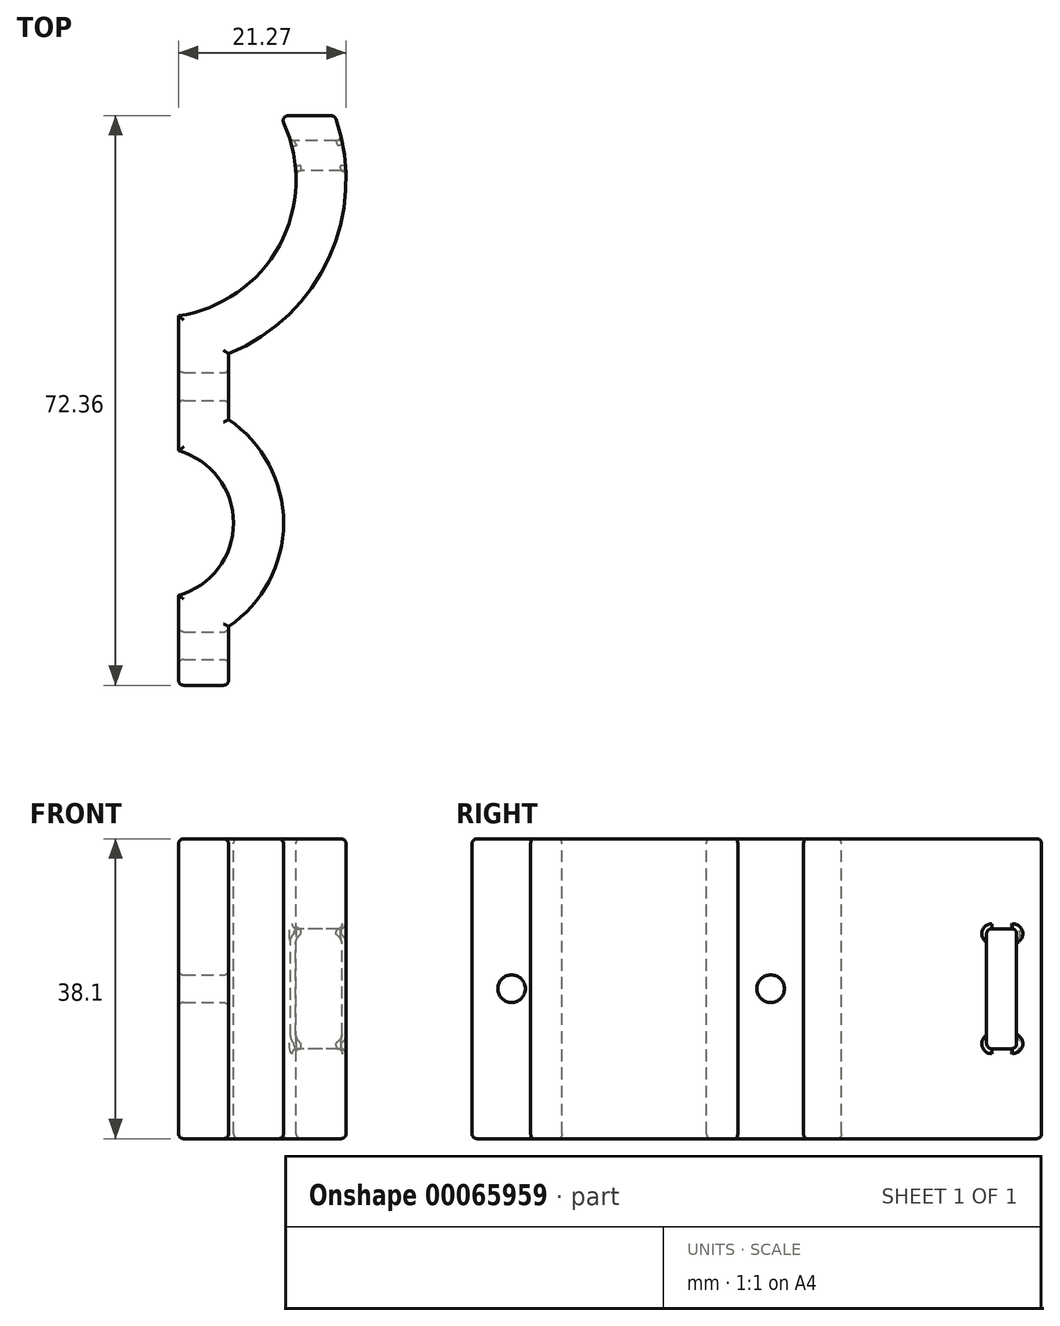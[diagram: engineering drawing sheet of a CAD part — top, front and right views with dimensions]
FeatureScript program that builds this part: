
annotation { "Feature Type Name" : "Feature", "Feature Type Description" : "" }
export const myFeature = defineFeature(function(context is Context, id is Id, definition is map)
    precondition{}
    {
        {
            var Q0;
            Q0=qCreatedBy(makeId("Top.planeOp"),FACE);
            var sketch = newSketch(context, id + "F0", { "sketchPlane" : qUnion([Q0])});
            skArc(sketch, "E0", {"start": v(0, 9.53) * mm, "mid": v(1.28, 9.44) * mm, "end": v(2.54, 9.18) * mm, "construction": true});
            skArc(sketch, "E1", {"start": v(0, 26.14) * mm, "mid": v(1.27, 26.19) * mm, "end": v(2.54, 26.33) * mm, "construction": true});
            skLineSegment(sketch, "E2", {"start": v(0, 43.6) * mm, "end": v(16.4, 49.57) * mm, "construction": true});
            skLineSegment(sketch, "E3", {"start": v(2.54, 26.33) * mm, "end": v(2.54, 9.18) * mm});
            skArc(sketch, "E4", {"start": v(16.4, 49.57) * mm, "mid": v(10.02, 57.9) * mm, "end": v(0, 61.06) * mm, "construction": true});
            skArc(sketch, "E5", {"start": v(2.54, 26.33) * mm, "mid": v(15.57, 35.7) * mm, "end": v(15.45, 51.75) * mm});
            skArc(sketch, "E6", {"start": v(2.54, 9.18) * mm, "mid": v(9.53, 0) * mm, "end": v(2.54, -9.18) * mm});
            skLineSegment(sketch, "E7", {"start": v(2.54, 9.18) * mm, "end": v(2.54, -9.18) * mm, "construction": true});
            skArc(sketch, "E8", {"start": v(2.54, -9.18) * mm, "mid": v(1.28, -9.44) * mm, "end": v(0, -9.53) * mm});
            skArc(sketch, "E9.0", {"start": v(8.9, 21.51) * mm, "mid": v(21.75, 33.9) * mm, "end": v(22.38, 51.75) * mm});
            skLineSegment(sketch, "E9.1", {"start": v(8.9, 21.51) * mm, "end": v(8.9, 13.15) * mm});
            skArc(sketch, "E9.2", {"start": v(8.9, 13.15) * mm, "mid": v(15.88, 0) * mm, "end": v(8.9, -13.15) * mm});
            skLineSegment(sketch, "E10", {"start": v(22.38, 51.75) * mm, "end": v(15.45, 51.75) * mm});
            skLineSegment(sketch, "E11", {"start": v(2.54, -9.18) * mm, "end": v(2.54, -20.61) * mm});
            skLineSegment(sketch, "E12.0", {"start": v(8.9, -13.15) * mm, "end": v(8.9, -20.61) * mm});
            skLineSegment(sketch, "E13", {"start": v(2.54, -20.61) * mm, "end": v(8.9, -20.61) * mm});
            skSolve(sketch);
        }
        {
            var Q0;
            Q0 = qSketchRegion(id + "F0", true);
            extrude(context, id + "F1", {"entities" : qUnion([Q0]), "oppositeDirection" : true, "depth" : 38.1 * mm});
        }
        {
            var Q0;
            Q0=makeQuery(id+"F1.opExtrude","SWEPT_FACE",FACE,{"disambiguationData":[OSD([sQuery(id+"F0.wireOp",EDGE,"E9.1")])]});
            var sketch = newSketch(context, id + "F2", { "sketchPlane" : qUnion([Q0])});
            skLineSegment(sketch, "E14", {"start": v(17.33, 0) * mm, "end": v(17.33, -38.1) * mm, "construction": true});
            skLineSegment(sketch, "E15", {"start": v(13.15, -19.05) * mm, "end": v(21.51, -19.05) * mm, "construction": true});
            skPoint(sketch, "E16", {"position": v(17.33, -19.05) * mm});
            skCircle(sketch, "E17", {"center": v(17.33, -19.05) * mm, "radius": 1.75 * mm});
            skSolve(sketch);
        }
        {
            var Q0;
            Q0 = qSketchRegion(id + "F2", true);
            extrude(context, id + "F3", {"entities" : qUnion([Q0]), "operationType" : NewBodyOperationType.REMOVE, "endBound" : BoundingType.UP_TO_NEXT, "oppositeDirection" : true, "depth" : 25.4 * mm});
        }
        {
            var Q0;
            Q0=qCreatedBy(makeId("Right.planeOp"),FACE);
            var sketch = newSketch(context, id + "F4", { "sketchPlane" : qUnion([Q0])});
            skLineSegment(sketch, "E18.0", {"start": v(21.51, 0) * mm, "end": v(21.51, -38.1) * mm, "construction": true});
            skLineSegment(sketch, "E19", {"start": v(71.82, -19.05) * mm, "end": v(21.51, -19.05) * mm, "construction": true});
            skPoint(sketch, "E19.endSnap0", {"position": v(21.51, -19.05) * mm});
            skLineSegment(sketch, "E20.rect.bottom", {"start": v(48.57, -11.43) * mm, "end": v(44.76, -11.43) * mm});
            skLineSegment(sketch, "E20.rect.top", {"start": v(48.57, -26.67) * mm, "end": v(44.76, -26.67) * mm});
            skLineSegment(sketch, "E20.rect.left", {"start": v(48.57, -11.43) * mm, "end": v(48.57, -26.67) * mm});
            skLineSegment(sketch, "E20.rect.right", {"start": v(44.76, -11.43) * mm, "end": v(44.76, -26.67) * mm});
            skPoint(sketch, "E20.rect.middle", {"position": v(46.67, -19.05) * mm});
            skSolve(sketch);
        }
        {
            var Q0;
            Q0 = qSketchRegion(id + "F4", true);
            extrude(context, id + "F5", {"entities" : qUnion([Q0]), "operationType" : NewBodyOperationType.REMOVE, "endBound" : BoundingType.THROUGH_ALL, "depth" : 25.4 * mm});
        }
        {
            var Q0;
            Q0=makeQuery(id+"F1.opExtrude","SWEPT_FACE",FACE,{"disambiguationData":[OSD([sQuery(id+"F0.wireOp",EDGE,"E12.0")])]});
            var sketch = newSketch(context, id + "F6", { "sketchPlane" : qUnion([Q0])});
            skLineSegment(sketch, "E21", {"start": v(-13.15, -19.05) * mm, "end": v(-13.15, -19.05) * mm});
            skLineSegment(sketch, "E22", {"start": v(-15.58, 0) * mm, "end": v(-15.58, -38.1) * mm, "construction": true});
            skPoint(sketch, "E23", {"position": v(-15.58, -19.05) * mm});
            skCircle(sketch, "E24", {"center": v(-15.58, -19.05) * mm, "radius": 1.75 * mm});
            skSolve(sketch);
        }
        {
            var Q0;
            Q0=makeQuery(id+"F6.imprint","IMPRINT",FACE,{"disambiguationData":[TD([[makeQuery(id+"F6.imprint","IMPRINT",EDGE,{"derivedFrom":sQuery(id+"F6.wireOp",EDGE,"E24")}),1.0]])]});
            var Q1;
            Q1=sQuery(id+"F6.wireOp",EDGE,"E24");
            extrude(context, id + "F7", {"entities" : qUnion([Q0]), "operationType" : NewBodyOperationType.REMOVE, "surfaceEntities" : qUnion([Q1]), "endBound" : BoundingType.THROUGH_ALL, "oppositeDirection" : true, "depth" : 25.4 * mm});
        }
        {
            var Q0;
            Q0=makeQuery(id+"F1.opExtrude","CAP_FACE",FACE,{"disambiguationData":[OSD([sQuery(id+"F0.wireOp",EDGE,"E3"),sQuery(id+"F0.wireOp",EDGE,"E5"),sQuery(id+"F0.wireOp",EDGE,"E6"),sQuery(id+"F0.wireOp",EDGE,"E9.0"),sQuery(id+"F0.wireOp",EDGE,"E9.1"),sQuery(id+"F0.wireOp",EDGE,"E9.2"),sQuery(id+"F0.wireOp",EDGE,"E10"),sQuery(id+"F0.wireOp",EDGE,"E11"),sQuery(id+"F0.wireOp",EDGE,"E12.0"),sQuery(id+"F0.wireOp",EDGE,"E13")])],"isStart":true});
            var Q1;
            Q1=makeQuery(id+"F1.opExtrude","CAP_FACE",FACE,{"disambiguationData":[OSD([sQuery(id+"F0.wireOp",EDGE,"E3"),sQuery(id+"F0.wireOp",EDGE,"E5"),sQuery(id+"F0.wireOp",EDGE,"E6"),sQuery(id+"F0.wireOp",EDGE,"E9.0"),sQuery(id+"F0.wireOp",EDGE,"E9.1"),sQuery(id+"F0.wireOp",EDGE,"E9.2"),sQuery(id+"F0.wireOp",EDGE,"E10"),sQuery(id+"F0.wireOp",EDGE,"E11"),sQuery(id+"F0.wireOp",EDGE,"E12.0"),sQuery(id+"F0.wireOp",EDGE,"E13")])],"isStart":false});
            var Q2;
            Q2=makeQuery(id+"F1.opExtrude","SWEPT_FACE",FACE,{"disambiguationData":[OSD([sQuery(id+"F0.wireOp",EDGE,"E13")])]});
            var Q3;
            Q3=makeQuery(id+"F1.opExtrude","SWEPT_FACE",FACE,{"disambiguationData":[OSD([sQuery(id+"F0.wireOp",EDGE,"E10")])]});
            var Q4;
            Q4=makeQuery(id+"F3.boolean.opBoolean","COPY",FACE,{"derivedFrom":makeQuery(id+"F3.opExtrude","SWEPT_FACE",FACE,{"disambiguationData":[OSD([sQuery(id+"F2.wireOp",EDGE,"E17")])]})});
            var Q5;
            Q5=makeQuery(id+"F7.boolean.opBoolean","COPY",FACE,{"derivedFrom":makeQuery(id+"F7.opExtrude","SWEPT_FACE",FACE,{"disambiguationData":[OSD([sQuery(id+"F6.wireOp",EDGE,"E24")])]})});
            var Q6;
            Q6=makeQuery(id+"F5.boolean.opBoolean","COPY",FACE,{"derivedFrom":makeQuery(id+"F5.opExtrude","SWEPT_FACE",FACE,{"disambiguationData":[OSD([sQuery(id+"F4.wireOp",EDGE,"E20.rect.bottom")])]})});
            var Q7;
            Q7=makeQuery(id+"F5.boolean.opBoolean","COPY",FACE,{"derivedFrom":makeQuery(id+"F5.opExtrude","SWEPT_FACE",FACE,{"disambiguationData":[OSD([sQuery(id+"F4.wireOp",EDGE,"E20.rect.top")])]})});
            fillet(context, id + "F8", {"entities" : qUnion([Q0, Q1, Q2, Q3, Q4, Q5, Q6, Q7]), "radius" : 0.64 * mm, "tangentPropagation" : true, "allowEdgeOverflow" : false});
        }
    });
